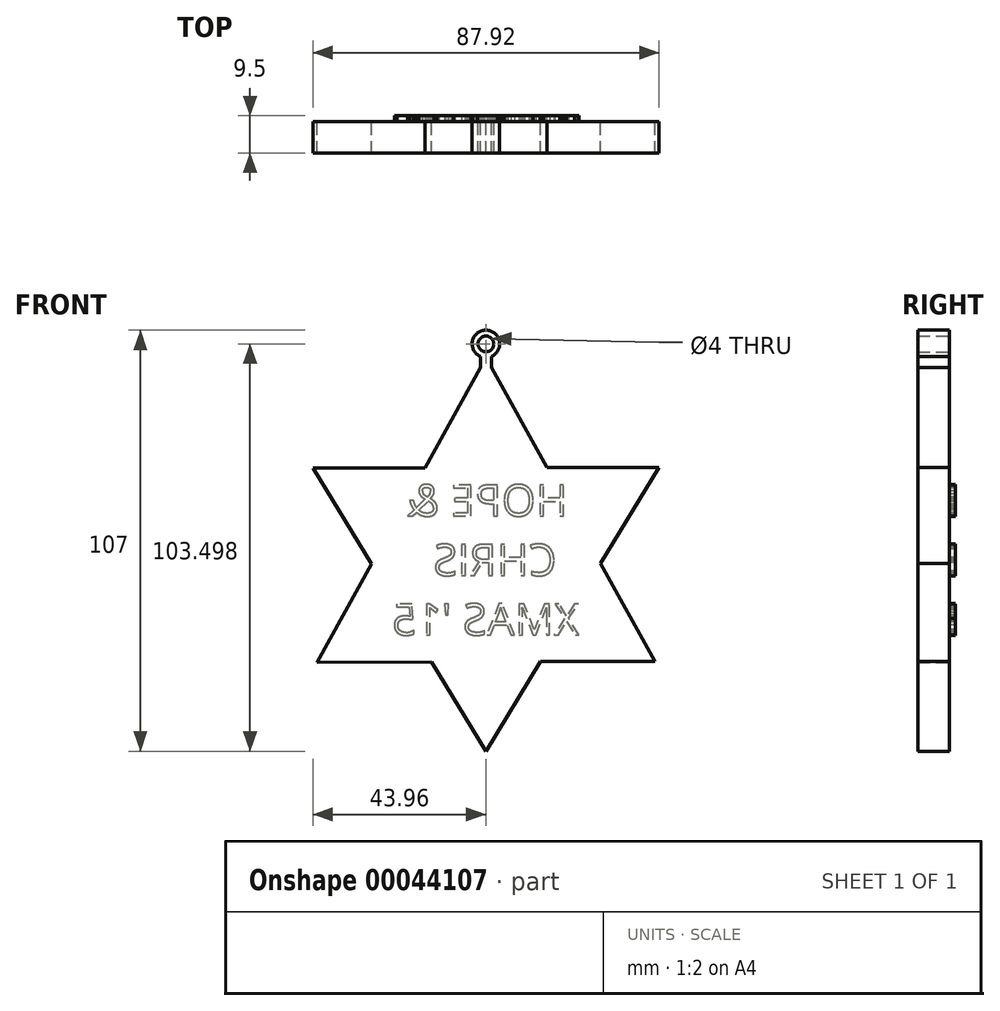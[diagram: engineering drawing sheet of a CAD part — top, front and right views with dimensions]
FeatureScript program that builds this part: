
annotation { "Feature Type Name" : "Feature", "Feature Type Description" : "" }
export const myFeature = defineFeature(function(context is Context, id is Id, definition is map)
    precondition{}
    {
        {
            var Q0;
            Q0=qCreatedBy(makeId("Front.planeOp"),FACE);
            var sketch = newSketch(context, id + "F0", { "sketchPlane" : qUnion([Q0])});
            skLineSegment(sketch, "E0.0", {"start": v(-43.96, 24.59) * mm, "end": v(-15.53, 24.66) * mm});
            skLineSegment(sketch, "E0.1", {"start": v(43.96, 24.8) * mm, "end": v(29.1, 0.43) * mm});
            skLineSegment(sketch, "E0.2", {"start": v(-1.37, -45.1) * mm, "end": v(-13.87, -24.65) * mm});
            skPoint(sketch, "E0.0.midPoint", {"position": v(0, 24.7) * mm});
            skLineSegment(sketch, "E1.0", {"start": v(1.4, 50.14) * mm, "end": v(15.56, 24.73) * mm});
            skLineSegment(sketch, "E1.1", {"start": v(43, -24.5) * mm, "end": v(13.87, -24.58) * mm});
            skLineSegment(sketch, "E1.2", {"start": v(-42.92, -24.72) * mm, "end": v(-29.08, 0.24) * mm});
            skPoint(sketch, "E1.0.midPoint", {"position": v(21.5, 14.08) * mm});
            skLineSegment(sketch, "E2.trimOffspring", {"start": v(-15.53, 24.66) * mm, "end": v(-1.4, 50.12) * mm});
            skLineSegment(sketch, "E3.trimOffspring", {"start": v(-29.08, 0.24) * mm, "end": v(-43.96, 24.59) * mm});
            skLineSegment(sketch, "E4.trimOffspring", {"start": v(-13.87, -24.65) * mm, "end": v(-42.92, -24.72) * mm});
            skLineSegment(sketch, "E5.trimOffspring", {"start": v(13.87, -24.58) * mm, "end": v(1.37, -45.1) * mm});
            skLineSegment(sketch, "E6.trimOffspring", {"start": v(29.1, 0.43) * mm, "end": v(43, -24.5) * mm});
            skLineSegment(sketch, "E7.trimOffspring", {"start": v(15.56, 24.73) * mm, "end": v(43.96, 24.8) * mm});
            skPoint(sketch, "E1.cCircle.center.orphan", {"position": v(0, 0) * mm});
            skLineSegment(sketch, "E8", {"start": v(-1.37, -45.1) * mm, "end": v(0, -47.34) * mm});
            skLineSegment(sketch, "E9", {"start": v(1.37, -45.1) * mm, "end": v(0, -47.34) * mm});
            skArc(sketch, "E10", {"start": v(1.4, 52.95) * mm, "mid": v(0, 59.66) * mm, "end": v(-1.4, 52.95) * mm});
            skCircle(sketch, "E11", {"center": v(0, 56.16) * mm, "radius": 2 * mm});
            skLineSegment(sketch, "E12", {"start": v(1.4, 52.95) * mm, "end": v(1.4, 50.14) * mm});
            skLineSegment(sketch, "E13", {"start": v(-1.4, 52.95) * mm, "end": v(-1.4, 50.12) * mm});
            skPoint(sketch, "E14.orphan", {"position": v(0, 52.66) * mm});
            skSolve(sketch);
        }
        {
            var Q0;
            Q0=makeQuery(id+"F0.imprint","IMPRINT",FACE,{"disambiguationData":[TD([[makeQuery(id+"F0.imprint","IMPRINT",EDGE,{"derivedFrom":sQuery(id+"F0.wireOp",EDGE,"E0.0")}),-1.0]])]});
            extrude(context, id + "F1", {"entities" : qUnion([Q0]), "depth" : 8 * mm});
        }
        {
            var Q0;
            Q0=makeQuery(id+"F1.opExtrude","CAP_FACE",FACE,{"disambiguationData":[OSD([sQuery(id+"F0.wireOp",EDGE,"E0.0"),sQuery(id+"F0.wireOp",EDGE,"E0.1"),sQuery(id+"F0.wireOp",EDGE,"E0.2"),sQuery(id+"F0.wireOp",EDGE,"E1.0"),sQuery(id+"F0.wireOp",EDGE,"E1.1"),sQuery(id+"F0.wireOp",EDGE,"E1.2"),sQuery(id+"F0.wireOp",EDGE,"acec650a-9a67-4413-bc85-cf65a41636c2"),sQuery(id+"F0.wireOp",EDGE,"1be782eb-550b-45c8-a2dc-cbf53aace19b"),sQuery(id+"F0.wireOp",EDGE,"E2.trimOffspring"),sQuery(id+"F0.wireOp",EDGE,"E3.trimOffspring"),sQuery(id+"F0.wireOp",EDGE,"E4.trimOffspring"),sQuery(id+"F0.wireOp",EDGE,"E5.trimOffspring"),sQuery(id+"F0.wireOp",EDGE,"E6.trimOffspring"),sQuery(id+"F0.wireOp",EDGE,"E7.trimOffspring"),sQuery(id+"F0.wireOp",EDGE,"4cdf7db9-103a-43ab-812f-f2832a3cbbde"),sQuery(id+"F0.wireOp",EDGE,"f8955658-ad1b-4e38-97dd-49a6fbd3d629")])],"isStart":true});
            var sketch = newSketch(context, id + "F2", { "sketchPlane" : qUnion([Q0])});
            skText(sketch, "E15", { "text": " HOPE & \n  CHRIS\nXMAS \'15", "fontName": "OpenSans-Regular.ttf"});
            const initialGuessF2  = {"E15": [-0.02371, 0.01243, 1, 0, 0.008]};
            skSetInitialGuess(sketch, initialGuessF2);
            skSolve(sketch);
        }
        {
            var Q0;
            Q0 = qSketchRegion(id + "F2", true);
            extrude(context, id + "F3", {"entities" : qUnion([Q0]), "operationType" : NewBodyOperationType.ADD, "depth" : 1.5 * mm});
        }
    });
